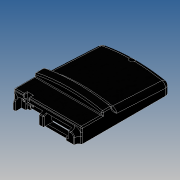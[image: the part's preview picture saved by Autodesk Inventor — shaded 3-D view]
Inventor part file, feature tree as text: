
AUTODESK INVENTOR PART (.ipt)
format: ipt  version: 2016 (Build 200138000, 138)  size: 730,112 bytes
history: native  units: mm
features: extrude x16, sketch x15, fillet x8, plane x2, direct_edit x2, move_body x2, shell x1, hole x1, chamfer x1, projected_geometry x1
ambient origin geometry x8: Origin, YZ Plane, XZ Plane, XY Plane, X Axis, Y Axis, Z Axis, Center Point
bodies: Solid1 (feature_tree)
feature tree (49):
  extrude  "Extrusion1"  Depth=150.0mm
  plane  "Work Plane2"
  extrude  "Extrusion2"  Depth=36.0mm
  sketch  "Sketch3"  dims[d9=30.0mm d10=16.5mm d11=0.0mm d13=-35.0mm d14=7.0mm]
  direct_edit  "Direct Edit1"
  extrude  "Extrusion3"  Depth=16.5mm TaperAngle=0.0deg
  fillet  "Fillet1"  [1 undecoded]
  fillet  "Fillet2"  Radius=7.0mm
  fillet  "Fillet3"  Radius=104.75mm
  shell  "Shell1"  Thickness=8.0mm
  extrude  "Extrusion4"  Depth=1.0mm
  fillet  "Fillet4"  Radius=3.0mm
  fillet  "Fillet5"  Radius=104.0mm
  fillet  "Fillet6"  Radius=16.0mm
  direct_edit  "Direct Edit2"
  sketch  "Sketch5"  dims[d21=2.0mm d22=1.0mm d23=3.0mm d24=104.0mm d25=16.0mm]
  extrude  "Extrusion5"  Depth=6.0mm
  extrude  "Extrusion6"  Depth=1.0mm
  extrude  "Extrusion7"  Depth=10.0mm
  extrude  "Extrusion8"  Depth=7.0mm
  extrude  "Extrusion9"  Depth=17.5mm
  fillet  "Fillet7"  Radius=8.5mm
  hole  "Hole1"  [1 undecoded]
  chamfer  "Chamfer1"  Distance=13.5mm
  extrude  "Extrusion10"  Depth=10.0mm TaperAngle=0.0deg
  fillet  "Fillet8"  Radius=28.0mm
  extrude  "Extrusion11"  Depth=10.0mm TaperAngle=0.0deg
  extrude  "Extrusion12"  Depth=8.0mm
  extrude  "Extrusion13"  Depth=2.8mm
  extrude  "Extrusion14"  Depth=2.8mm
  extrude  "Extrusion15"  Depth=2.8mm
  plane  "Work Plane3"
  extrude  "Extrusion16"  Depth=2.8mm TaperAngle=0.0deg
  sketch  "Sketch1"  dims[d0=115.0mm d1=150.0mm]
  sketch  "Sketch2"  dims[d2=25.0mm d3=0.0mm d8=36.0mm]
  sketch  "Sketch4"  dims[d15=0.0mm d16=0.0mm d17=5.0mm d18=104.75mm d19=0.523599mm d20=8.0mm]
  sketch  "Sketch6"  dims[d26=7.0mm d27=0.0mm d28=6.0mm]
  sketch  "Sketch7"  dims[d29=1.5mm d30=1.0mm]
  sketch  "Sketch8"  dims[d31=10.0mm d32=42.0mm]
  sketch  "Sketch9"  dims[d34=14.0mm d35=7.0mm]
  sketch  "Sketch11"  dims[d36=37.3mm d37=17.5mm d38=8.5mm]
  sketch  "Sketch12"  dims[d39=10.5mm d40=39.0mm d41=13.5mm d42=0.0mm]
  sketch  "Sketch13"  dims[d43=0.0mm d44=0.0mm d45=6.0mm d46=10.0mm d47=0.0mm d48=28.0mm]
  sketch  "Sketch14"  dims[d49=7.5mm d50=10.0mm d51=0.0mm]
  sketch  "Sketch15"  dims[d52=51.0mm d53=8.0mm]
  projected_geometry  "Projected Loop1"
  sketch  "Sketch16"  dims[d54=5.0mm d55=0.0mm d56=1.5mm d57=0.5mm d58=7.0mm d59=2.0mm d60=0.0mm d61=1.0mm d62=15.0mm d63=2.459mm d64=6.0mm d65=4.0mm d66=2.0mm d67=90.0deg d68=8.8mm d69=20.594885mm d70=0.5mm d71=2.0mm d72=45.0deg d73=22.8mm d74=14.0mm d75=9.0mm d76=7.0mm d77=0.0mm d78=5.0mm d79=2.0mm d80=1.0mm d81=2.0mm d82=1.0mm d83=6.0mm d84=8.0mm d85=10.0mm d86=1.5mm d87=0.0mm d88=12.8mm d89=14.5mm d90=1.5mm d91=0.0mm d92=3.0mm d93=1.8mm d94=0.0mm d95=68.0mm d96=3.5mm d97=1.8mm d98=0.0mm d99=9.0mm d100=1.8mm d101=0.0mm d102=2.5mm d103=10.0mm d104=10.0mm d105=10.0mm d106=2.8mm d107=14.0mm d108=32.0mm d109=45.0mm d110=1.8mm d111=0.0mm]
  move_body  "Move1"
  move_body  "Move2"
note: 2 required parameter values undecoded (feature->parameter linkage not recoverable at this tier; creation-order binding heuristic only, values carry confidence <= 0.55)
